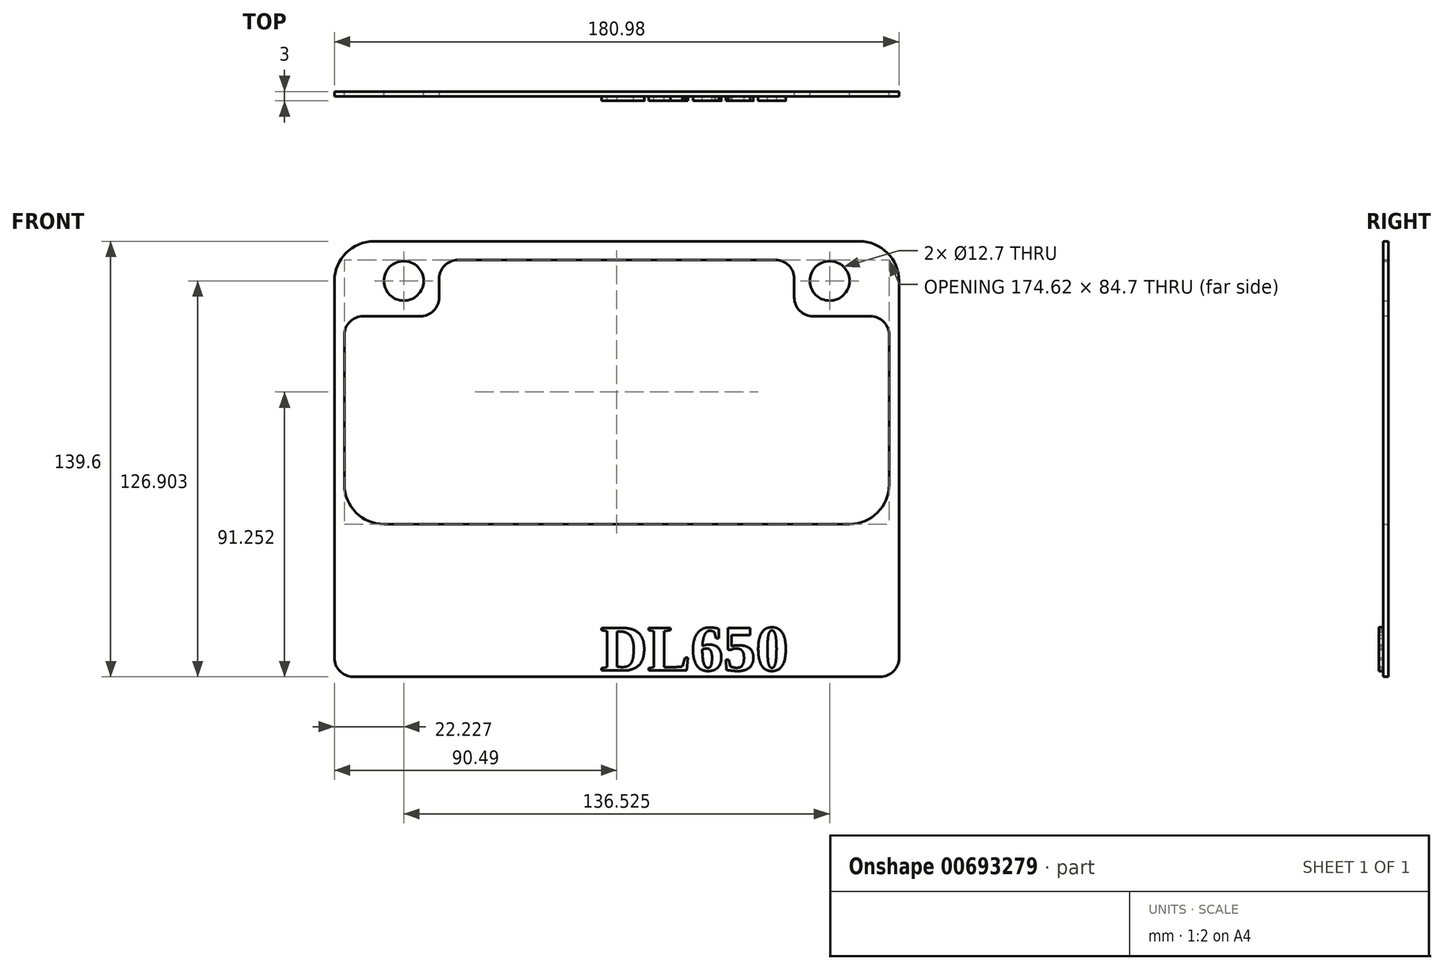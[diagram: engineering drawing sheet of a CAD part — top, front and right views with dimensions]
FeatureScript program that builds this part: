
annotation { "Feature Type Name" : "Feature", "Feature Type Description" : "" }
export const myFeature = defineFeature(function(context is Context, id is Id, definition is map)
    precondition{}
    {
        {
            var Q0;
            Q0=qCreatedBy(makeId("Front.planeOp"),FACE);
            var sketch = newSketch(context, id + "F0", { "sketchPlane" : qUnion([Q0])});
            skLineSegment(sketch, "E0", {"start": v(-77.79, 78) * mm, "end": v(77.79, 78) * mm});
            skLineSegment(sketch, "E1", {"start": v(-74.61, 44) * mm, "end": v(74.61, 44) * mm});
            skLineSegment(sketch, "E2", {"start": v(-90.49, -68.18) * mm, "end": v(-90.49, 65.3) * mm});
            skLineSegment(sketch, "E3", {"start": v(90.49, 65.3) * mm, "end": v(90.49, -55.07) * mm});
            skLineSegment(sketch, "E4", {"start": v(87.31, 31.3) * mm, "end": v(87.31, 0) * mm});
            skLineSegment(sketch, "E5", {"start": v(-87.31, -61.26) * mm, "end": v(-87.31, -36.3) * mm});
            skLineSegment(sketch, "E6", {"start": v(-29.21, -51.66) * mm, "end": v(-23.1, -50.51) * mm});
            skLineSegment(sketch, "E7", {"start": v(-23.1, -50.51) * mm, "end": v(-20.29, -50.51) * mm});
            skLineSegment(sketch, "E8", {"start": v(-20.29, -50.51) * mm, "end": v(-18.64, -50.51) * mm});
            skLineSegment(sketch, "E9", {"start": v(-18.64, -50.51) * mm, "end": v(-22.38, -52.6) * mm});
            skLineSegment(sketch, "E10", {"start": v(-22.38, -52.6) * mm, "end": v(-28.52, -54.74) * mm});
            skLineSegment(sketch, "E11", {"start": v(-28.52, -54.74) * mm, "end": v(-35.07, -55.94) * mm});
            skLineSegment(sketch, "E12", {"start": v(-35.07, -55.94) * mm, "end": v(-35.07, -58.79) * mm});
            skLineSegment(sketch, "E13", {"start": v(-35.07, -58.79) * mm, "end": v(-27.72, -61.77) * mm});
            skLineSegment(sketch, "E14", {"start": v(-27.72, -61.77) * mm, "end": v(-24.39, -63.12) * mm});
            skLineSegment(sketch, "E15", {"start": v(-24.39, -63.12) * mm, "end": v(-22.78, -62.57) * mm});
            skLineSegment(sketch, "E16", {"start": v(-22.78, -62.57) * mm, "end": v(-14.86, -59.1) * mm});
            skLineSegment(sketch, "E17", {"start": v(-14.86, -59.1) * mm, "end": v(-13.34, -57.8) * mm});
            skLineSegment(sketch, "E18", {"start": v(-13.34, -57.8) * mm, "end": v(-20.87, -57.8) * mm});
            skLineSegment(sketch, "E19", {"start": v(-20.87, -57.8) * mm, "end": v(-20.87, -55.05) * mm});
            skLineSegment(sketch, "E20", {"start": v(-20.87, -55.05) * mm, "end": v(-9.3, -55.27) * mm});
            skLineSegment(sketch, "E21", {"start": v(-9.3, -55.27) * mm, "end": v(-5.99, -52.6) * mm});
            skLineSegment(sketch, "E22", {"start": v(-5.99, -52.6) * mm, "end": v(-2.52, -52.6) * mm});
            skLineSegment(sketch, "E23", {"start": v(-2.52, -52.6) * mm, "end": v(-2.32, -55) * mm});
            skLineSegment(sketch, "E24", {"start": v(-2.32, -55) * mm, "end": v(2.72, -55) * mm});
            skLineSegment(sketch, "E25", {"start": v(2.72, -55) * mm, "end": v(1.05, -57.08) * mm});
            skLineSegment(sketch, "E26", {"start": v(1.05, -57.08) * mm, "end": v(-3.5, -57.08) * mm});
            skLineSegment(sketch, "E27", {"start": v(-3.5, -57.08) * mm, "end": v(-8.64, -62.21) * mm});
            skLineSegment(sketch, "E28", {"start": v(-8.64, -62.21) * mm, "end": v(-8.64, -63.64) * mm});
            skLineSegment(sketch, "E29", {"start": v(-8.64, -63.64) * mm, "end": v(-6.69, -63.64) * mm});
            skLineSegment(sketch, "E30", {"start": v(-6.69, -63.64) * mm, "end": v(2.22, -59.94) * mm});
            skLineSegment(sketch, "E31", {"start": v(2.22, -59.94) * mm, "end": v(5.6, -59.25) * mm});
            skLineSegment(sketch, "E32", {"start": v(5.6, -59.25) * mm, "end": v(12.9, -59.62) * mm});
            skLineSegment(sketch, "E33", {"start": v(12.9, -59.62) * mm, "end": v(13.98, -60.58) * mm});
            skLineSegment(sketch, "E34", {"start": v(13.98, -60.58) * mm, "end": v(13, -62.78) * mm});
            skLineSegment(sketch, "E35", {"start": v(13, -62.78) * mm, "end": v(12.55, -63.82) * mm});
            skLineSegment(sketch, "E36", {"start": v(12.55, -63.82) * mm, "end": v(13.6, -63.82) * mm});
            skLineSegment(sketch, "E37", {"start": v(13.6, -63.82) * mm, "end": v(15.7, -63.82) * mm});
            skLineSegment(sketch, "E38", {"start": v(15.7, -63.82) * mm, "end": v(22.1, -60.67) * mm});
            skLineSegment(sketch, "E39", {"start": v(22.1, -60.67) * mm, "end": v(24.65, -59.78) * mm});
            skLineSegment(sketch, "E40", {"start": v(24.65, -59.78) * mm, "end": v(27.62, -59.78) * mm});
            skLineSegment(sketch, "E41", {"start": v(27.62, -59.78) * mm, "end": v(30.1, -59.78) * mm});
            skLineSegment(sketch, "E42", {"start": v(30.1, -59.78) * mm, "end": v(31.7, -60) * mm});
            skLineSegment(sketch, "E43", {"start": v(29.74, -61.98) * mm, "end": v(27.27, -61.82) * mm});
            skLineSegment(sketch, "E44", {"start": v(27.27, -61.82) * mm, "end": v(25.05, -62.7) * mm});
            skLineSegment(sketch, "E45", {"start": v(25.05, -62.7) * mm, "end": v(23.07, -63.82) * mm});
            skLineSegment(sketch, "E46", {"start": v(23.07, -63.82) * mm, "end": v(23.07, -64.66) * mm});
            skLineSegment(sketch, "E47", {"start": v(23.07, -64.66) * mm, "end": v(23.64, -65.45) * mm});
            skLineSegment(sketch, "E48", {"start": v(23.64, -65.45) * mm, "end": v(24.65, -65.45) * mm});
            skLineSegment(sketch, "E49", {"start": v(24.65, -65.45) * mm, "end": v(27.23, -65.45) * mm});
            skLineSegment(sketch, "E50", {"start": v(27.23, -65.45) * mm, "end": v(28.75, -65.45) * mm});
            skLineSegment(sketch, "E51", {"start": v(28.75, -65.45) * mm, "end": v(28.75, -65.45) * mm});
            skLineSegment(sketch, "E52", {"start": v(28.75, -65.45) * mm, "end": v(30.56, -64.83) * mm});
            skLineSegment(sketch, "E53", {"start": v(30.56, -64.83) * mm, "end": v(31.39, -63.37) * mm});
            skLineSegment(sketch, "E54", {"start": v(31.39, -63.37) * mm, "end": v(30.32, -62.47) * mm});
            skLineSegment(sketch, "E55", {"start": v(30.32, -62.47) * mm, "end": v(29.74, -61.98) * mm});
            skLineSegment(sketch, "E56", {"start": v(31.7, -60) * mm, "end": v(37.4, -60) * mm});
            skLineSegment(sketch, "E57", {"start": v(37.4, -60) * mm, "end": v(38.4, -61.18) * mm});
            skLineSegment(sketch, "E58", {"start": v(38.4, -61.18) * mm, "end": v(39.02, -62.98) * mm});
            skLineSegment(sketch, "E59", {"start": v(39.02, -62.98) * mm, "end": v(39.02, -63.65) * mm});
            skLineSegment(sketch, "E60", {"start": v(39.02, -63.65) * mm, "end": v(41.33, -62.76) * mm});
            skLineSegment(sketch, "E61", {"start": v(41.33, -62.76) * mm, "end": v(44.09, -61.68) * mm});
            skLineSegment(sketch, "E62", {"start": v(44.09, -61.68) * mm, "end": v(47.27, -60.44) * mm});
            skLineSegment(sketch, "E63", {"start": v(47.27, -60.44) * mm, "end": v(50.76, -59.08) * mm});
            skLineSegment(sketch, "E64", {"start": v(50.76, -59.08) * mm, "end": v(54.5, -59.08) * mm});
            skLineSegment(sketch, "E65", {"start": v(54.5, -59.08) * mm, "end": v(54.6, -61.64) * mm});
            skLineSegment(sketch, "E66", {"start": v(54.6, -61.64) * mm, "end": v(54.63, -62.25) * mm});
            skLineSegment(sketch, "E67", {"start": v(54.63, -62.25) * mm, "end": v(61.4, -59.33) * mm});
            skLineSegment(sketch, "E68", {"start": v(61.4, -59.33) * mm, "end": v(63.14, -58.58) * mm});
            skLineSegment(sketch, "E69", {"start": v(63.14, -58.58) * mm, "end": v(66.16, -58.58) * mm});
            skLineSegment(sketch, "E70", {"start": v(66.16, -58.58) * mm, "end": v(67, -58.91) * mm});
            skLineSegment(sketch, "E71", {"start": v(67, -58.91) * mm, "end": v(67, -60.93) * mm});
            skLineSegment(sketch, "E72", {"start": v(67, -60.93) * mm, "end": v(67, -61.6) * mm});
            skLineSegment(sketch, "E73", {"start": v(67, -61.6) * mm, "end": v(67, -62.28) * mm});
            skLineSegment(sketch, "E74", {"start": v(67, -62.28) * mm, "end": v(75.87, -58.62) * mm});
            skLineSegment(sketch, "E75", {"start": v(75.87, -58.62) * mm, "end": v(78.57, -58.62) * mm});
            skLineSegment(sketch, "E76", {"start": v(78.57, -58.62) * mm, "end": v(78.57, -61.4) * mm});
            skLineSegment(sketch, "E77", {"start": v(78.57, -61.4) * mm, "end": v(77.64, -63.25) * mm});
            skLineSegment(sketch, "E78", {"start": v(77.64, -63.25) * mm, "end": v(80.4, -62.97) * mm});
            skLineSegment(sketch, "E79", {"start": v(80.4, -62.97) * mm, "end": v(80.4, -62.97) * mm});
            skLineSegment(sketch, "E80", {"start": v(-82, -51.28) * mm, "end": v(-82, -52.51) * mm});
            skLineSegment(sketch, "E81", {"start": v(-82, -52.51) * mm, "end": v(-85.85, -58.12) * mm});
            skLineSegment(sketch, "E82", {"start": v(-85.85, -58.12) * mm, "end": v(-87.31, -61.26) * mm});
            skLineSegment(sketch, "E83", {"start": v(-80.53, -66.46) * mm, "end": v(-80.53, -67.97) * mm});
            skArc(sketch, "E84", {"start": v(-80.53, -67.6) * mm, "mid": v(-80.07, -68.53) * mm, "end": v(-79.07, -68.25) * mm});
            skLineSegment(sketch, "E85", {"start": v(-79.07, -68.25) * mm, "end": v(-73.01, -63.37) * mm});
            skLineSegment(sketch, "E86", {"start": v(-73.01, -63.37) * mm, "end": v(-64.95, -57.96) * mm});
            skLineSegment(sketch, "E87", {"start": v(-64.95, -57.96) * mm, "end": v(-56.54, -52.32) * mm});
            skLineSegment(sketch, "E88", {"start": v(-56.54, -52.32) * mm, "end": v(-43.18, -46.47) * mm});
            skLineSegment(sketch, "E89", {"start": v(-43.18, -46.47) * mm, "end": v(-41.77, -46.08) * mm});
            skLineSegment(sketch, "E90", {"start": v(-41.77, -46.08) * mm, "end": v(-38.67, -45.2) * mm});
            skLineSegment(sketch, "E91", {"start": v(-38.67, -45.2) * mm, "end": v(-31.98, -45.2) * mm});
            skLineSegment(sketch, "E92", {"start": v(-31.98, -45.2) * mm, "end": v(-31.98, -46.08) * mm});
            skLineSegment(sketch, "E93", {"start": v(-31.98, -46.08) * mm, "end": v(-37.08, -47.84) * mm});
            skLineSegment(sketch, "E94", {"start": v(-37.08, -47.84) * mm, "end": v(-42.97, -49.87) * mm});
            skLineSegment(sketch, "E95", {"start": v(-42.97, -49.87) * mm, "end": v(-54.97, -57.27) * mm});
            skLineSegment(sketch, "E96", {"start": v(-54.97, -57.27) * mm, "end": v(-58.2, -60.02) * mm});
            skLineSegment(sketch, "E97", {"start": v(-58.2, -60.02) * mm, "end": v(-58.2, -61.31) * mm});
            skLineSegment(sketch, "E98", {"start": v(-58.2, -61.31) * mm, "end": v(-49.34, -61.31) * mm});
            skLineSegment(sketch, "E99", {"start": v(-56.96, -68.6) * mm, "end": v(-54.55, -68.27) * mm});
            skLineSegment(sketch, "E100", {"start": v(-85.54, -78) * mm, "end": v(-81.5, -78) * mm});
            skLineSegment(sketch, "E101", {"start": v(-90.39, -73.88) * mm, "end": v(-85.54, -77.1) * mm});
            skLineSegment(sketch, "E102", {"start": v(-85.54, -77.1) * mm, "end": v(-85.54, -78) * mm});
            skLineSegment(sketch, "E103", {"start": v(-84.43, -51.28) * mm, "end": v(-84.43, -49.97) * mm});
            skLineSegment(sketch, "E104", {"start": v(-84.43, -49.97) * mm, "end": v(-76.06, -46.38) * mm});
            skLineSegment(sketch, "E105", {"start": v(-76.06, -46.38) * mm, "end": v(-70.01, -46.38) * mm});
            skLineSegment(sketch, "E106", {"start": v(-70, -48.96) * mm, "end": v(-80.53, -66.46) * mm});
            skLineSegment(sketch, "E107", {"start": v(-84.43, -51.28) * mm, "end": v(-82, -51.28) * mm});
            skArc(sketch, "E108", {"start": v(-70, -48.96) * mm, "mid": v(-69.56, -47.67) * mm, "end": v(-70.01, -46.38) * mm});
            skLineSegment(sketch, "E109", {"start": v(-33.04, -63.57) * mm, "end": v(-42.47, -59.8) * mm});
            skLineSegment(sketch, "E110", {"start": v(-45.02, -57.68) * mm, "end": v(-43.38, -56.24) * mm});
            skLineSegment(sketch, "E111", {"start": v(-43.38, -56.24) * mm, "end": v(-38.17, -53.84) * mm});
            skLineSegment(sketch, "E112", {"start": v(-38.17, -53.84) * mm, "end": v(-32.55, -52.47) * mm});
            skLineSegment(sketch, "E113", {"start": v(-32.55, -52.47) * mm, "end": v(-29.21, -51.66) * mm});
            skArc(sketch, "E114", {"start": v(-45.02, -57.68) * mm, "mid": v(-43.94, -58.96) * mm, "end": v(-42.47, -59.8) * mm});
            skArc(sketch, "E115", {"start": v(-32.75, -65.3) * mm, "mid": v(-32.5, -64.25) * mm, "end": v(-33.27, -63.48) * mm});
            skLineSegment(sketch, "E116", {"start": v(82.78, -65.37) * mm, "end": v(76.07, -67.34) * mm});
            skLineSegment(sketch, "E117", {"start": v(76.07, -67.34) * mm, "end": v(71.6, -67.34) * mm});
            skLineSegment(sketch, "E118", {"start": v(71.6, -67.34) * mm, "end": v(72.25, -63.16) * mm});
            skLineSegment(sketch, "E119", {"start": v(72.25, -63.16) * mm, "end": v(62.42, -66.98) * mm});
            skLineSegment(sketch, "E120", {"start": v(62.42, -66.98) * mm, "end": v(57.9, -66.98) * mm});
            skLineSegment(sketch, "E121", {"start": v(57.9, -66.98) * mm, "end": v(59.54, -64.28) * mm});
            skLineSegment(sketch, "E122", {"start": v(59.54, -64.28) * mm, "end": v(58.84, -63.4) * mm});
            skLineSegment(sketch, "E123", {"start": v(58.84, -63.4) * mm, "end": v(57.37, -63.4) * mm});
            skLineSegment(sketch, "E124", {"start": v(57.37, -63.4) * mm, "end": v(49.3, -67.45) * mm});
            skLineSegment(sketch, "E125", {"start": v(49.3, -67.45) * mm, "end": v(45.66, -67.45) * mm});
            skLineSegment(sketch, "E126", {"start": v(45.66, -67.45) * mm, "end": v(44.96, -65.99) * mm});
            skLineSegment(sketch, "E127", {"start": v(44.96, -65.99) * mm, "end": v(46.72, -64.4) * mm});
            skLineSegment(sketch, "E128", {"start": v(46.72, -64.4) * mm, "end": v(46.43, -63.45) * mm});
            skLineSegment(sketch, "E129", {"start": v(46.43, -63.45) * mm, "end": v(45.22, -63.45) * mm});
            skLineSegment(sketch, "E130", {"start": v(45.22, -63.45) * mm, "end": v(41.02, -65.5) * mm});
            skLineSegment(sketch, "E131", {"start": v(41.02, -65.5) * mm, "end": v(39.57, -66.2) * mm});
            skLineSegment(sketch, "E132", {"start": v(39.57, -66.2) * mm, "end": v(37.64, -67.14) * mm});
            skLineSegment(sketch, "E133", {"start": v(37.64, -67.14) * mm, "end": v(31, -67.9) * mm});
            skLineSegment(sketch, "E134", {"start": v(31, -67.9) * mm, "end": v(27.87, -68.25) * mm});
            skLineSegment(sketch, "E135", {"start": v(27.87, -68.25) * mm, "end": v(22.36, -68.25) * mm});
            skLineSegment(sketch, "E136", {"start": v(22.36, -68.25) * mm, "end": v(20.07, -68.25) * mm});
            skLineSegment(sketch, "E137", {"start": v(20.07, -68.25) * mm, "end": v(18.41, -66.61) * mm});
            skLineSegment(sketch, "E138", {"start": v(18.41, -66.61) * mm, "end": v(17.72, -65.92) * mm});
            skLineSegment(sketch, "E139", {"start": v(17.72, -65.92) * mm, "end": v(16.92, -65.92) * mm});
            skLineSegment(sketch, "E140", {"start": v(16.92, -65.92) * mm, "end": v(14.63, -65.92) * mm});
            skLineSegment(sketch, "E141", {"start": v(14.63, -65.92) * mm, "end": v(7.74, -67.52) * mm});
            skLineSegment(sketch, "E142", {"start": v(7.74, -67.52) * mm, "end": v(6.36, -67.52) * mm});
            skLineSegment(sketch, "E143", {"start": v(6.36, -67.52) * mm, "end": v(6.36, -65.44) * mm});
            skLineSegment(sketch, "E144", {"start": v(6.36, -65.44) * mm, "end": v(7.32, -64.7) * mm});
            skLineSegment(sketch, "E145", {"start": v(7.32, -64.7) * mm, "end": v(8.44, -63.84) * mm});
            skLineSegment(sketch, "E146", {"start": v(8.44, -63.84) * mm, "end": v(8.38, -62.61) * mm});
            skLineSegment(sketch, "E147", {"start": v(8.38, -62.61) * mm, "end": v(6.68, -62.03) * mm});
            skLineSegment(sketch, "E148", {"start": v(6.68, -62.03) * mm, "end": v(4.17, -62.03) * mm});
            skLineSegment(sketch, "E149", {"start": v(4.17, -62.03) * mm, "end": v(0.97, -63.79) * mm});
            skLineSegment(sketch, "E150", {"start": v(0.97, -63.79) * mm, "end": v(-9.74, -67.36) * mm});
            skLineSegment(sketch, "E151", {"start": v(-9.74, -67.36) * mm, "end": v(-12.94, -67.36) * mm});
            skLineSegment(sketch, "E152", {"start": v(-12.94, -67.36) * mm, "end": v(-15.34, -67.36) * mm});
            skLineSegment(sketch, "E153", {"start": v(-15.34, -67.36) * mm, "end": v(-15.34, -62.83) * mm});
            skLineSegment(sketch, "E154", {"start": v(-15.34, -62.83) * mm, "end": v(-15.98, -62.83) * mm});
            skLineSegment(sketch, "E155", {"start": v(-15.98, -62.83) * mm, "end": v(-20.25, -64.96) * mm});
            skLineSegment(sketch, "E156", {"start": v(-20.25, -64.96) * mm, "end": v(-34.94, -68.98) * mm});
            skLineSegment(sketch, "E157", {"start": v(-34.94, -68.98) * mm, "end": v(-42.63, -70.75) * mm});
            skLineSegment(sketch, "E158", {"start": v(-42.63, -70.75) * mm, "end": v(-45.78, -71.48) * mm});
            skLineSegment(sketch, "E159", {"start": v(-45.78, -71.48) * mm, "end": v(-48.87, -72.2) * mm});
            skLineSegment(sketch, "E160", {"start": v(-48.87, -72.2) * mm, "end": v(-53.53, -71.11) * mm});
            skLineSegment(sketch, "E161", {"start": v(-53.53, -71.11) * mm, "end": v(-56.96, -68.6) * mm});
            skLineSegment(sketch, "E162", {"start": v(-90.49, -68.18) * mm, "end": v(-90.39, -73.88) * mm});
            skCircle(sketch, "E163", {"center": v(-68.26, 65.3) * mm, "radius": 6.35 * mm});
            skCircle(sketch, "E164", {"center": v(68.26, 65.3) * mm, "radius": 6.35 * mm});
            skLineSegment(sketch, "E165", {"start": v(-54.55, -64.45) * mm, "end": v(-54.55, -68.27) * mm});
            skLineSegment(sketch, "E166", {"start": v(-49.34, -61.31) * mm, "end": v(-49.34, -67.56) * mm});
            skLineSegment(sketch, "E167", {"start": v(-54.55, -64.45) * mm, "end": v(-59.25, -64.45) * mm});
            skLineSegment(sketch, "E168", {"start": v(-59.25, -64.45) * mm, "end": v(-62.72, -64.2) * mm});
            skLineSegment(sketch, "E169", {"start": v(-62.72, -64.2) * mm, "end": v(-63.8, -64.11) * mm});
            skLineSegment(sketch, "E170", {"start": v(-63.8, -64.11) * mm, "end": v(-79.82, -76.84) * mm});
            skLineSegment(sketch, "E171", {"start": v(-79.82, -76.84) * mm, "end": v(-81.5, -78) * mm});
            skLineSegment(sketch, "E172", {"start": v(-49.34, -67.56) * mm, "end": v(-32.75, -65.3) * mm});
            skArc(sketch, "E173", {"start": v(-74.61, 44) * mm, "mid": v(-83.6, 40.29) * mm, "end": v(-87.31, 31.3) * mm});
            skArc(sketch, "E174", {"start": v(87.31, 31.3) * mm, "mid": v(83.6, 40.29) * mm, "end": v(74.61, 44) * mm});
            skArc(sketch, "E175", {"start": v(-77.79, 78) * mm, "mid": v(-86.77, 74.28) * mm, "end": v(-90.49, 65.3) * mm});
            skArc(sketch, "E176", {"start": v(90.49, 65.3) * mm, "mid": v(86.77, 74.28) * mm, "end": v(77.79, 78) * mm});
            skLineSegment(sketch, "E177", {"start": v(-74.61, -23.6) * mm, "end": v(74.61, -23.6) * mm});
            skLineSegment(sketch, "E178", {"start": v(-74.61, -12.7) * mm, "end": v(74.61, -12.7) * mm});
            skLineSegment(sketch, "E179", {"start": v(-87.31, 0) * mm, "end": v(-87.31, 31.3) * mm});
            skLineSegment(sketch, "E180", {"start": v(87.31, -36.3) * mm, "end": v(87.31, -53.65) * mm});
            skArc(sketch, "E181", {"start": v(-87.31, 0) * mm, "mid": v(-83.6, -8.98) * mm, "end": v(-74.61, -12.7) * mm});
            skArc(sketch, "E182", {"start": v(-74.61, -23.6) * mm, "mid": v(-83.6, -27.32) * mm, "end": v(-87.31, -36.3) * mm});
            skArc(sketch, "E183", {"start": v(87.31, -36.3) * mm, "mid": v(83.6, -27.32) * mm, "end": v(74.61, -23.6) * mm});
            skArc(sketch, "E184", {"start": v(74.61, -12.7) * mm, "mid": v(83.6, -8.98) * mm, "end": v(87.31, 0) * mm});
            skLineSegment(sketch, "E185", {"start": v(0, 78) * mm, "end": v(0, 44) * mm, "construction": true});
            skLineSegment(sketch, "E186", {"start": v(0, 0) * mm, "end": v(0, -23.6) * mm, "construction": true});
            skArc(sketch, "E187", {"start": v(80.4, -62.97) * mm, "mid": v(85.4, -59.45) * mm, "end": v(87.31, -53.65) * mm});
            skArc(sketch, "E188", {"start": v(82.78, -65.37) * mm, "mid": v(88.35, -61.5) * mm, "end": v(90.49, -55.07) * mm});
            skSolve(sketch);
        }
        {
            var Q0;
            Q0 = qSketchRegion(id + "F0", true);
            extrude(context, id + "F1", {"entities" : qUnion([Q0]), "depth" : 1.6 * mm, "offsetDistance" : 25 * mm});
        }
        {
            var Q0;
            Q0=makeQuery(id+"F1.opExtrude","CAP_FACE",FACE,{"disambiguationData":[OSD([sQuery(id+"F0.wireOp",EDGE,"E0"),sQuery(id+"F0.wireOp",EDGE,"E1"),sQuery(id+"F0.wireOp",EDGE,"E2"),sQuery(id+"F0.wireOp",EDGE,"E3"),sQuery(id+"F0.wireOp",EDGE,"E4"),sQuery(id+"F0.wireOp",EDGE,"E5"),sQuery(id+"F0.wireOp",EDGE,"E6"),sQuery(id+"F0.wireOp",EDGE,"E7"),sQuery(id+"F0.wireOp",EDGE,"E8"),sQuery(id+"F0.wireOp",EDGE,"E9"),sQuery(id+"F0.wireOp",EDGE,"E10"),sQuery(id+"F0.wireOp",EDGE,"E11"),sQuery(id+"F0.wireOp",EDGE,"E12"),sQuery(id+"F0.wireOp",EDGE,"E13"),sQuery(id+"F0.wireOp",EDGE,"E14"),sQuery(id+"F0.wireOp",EDGE,"E15"),sQuery(id+"F0.wireOp",EDGE,"E16"),sQuery(id+"F0.wireOp",EDGE,"E17"),sQuery(id+"F0.wireOp",EDGE,"E18"),sQuery(id+"F0.wireOp",EDGE,"E19"),sQuery(id+"F0.wireOp",EDGE,"E20"),sQuery(id+"F0.wireOp",EDGE,"E21"),sQuery(id+"F0.wireOp",EDGE,"E22"),sQuery(id+"F0.wireOp",EDGE,"E23"),sQuery(id+"F0.wireOp",EDGE,"E24"),sQuery(id+"F0.wireOp",EDGE,"E25"),sQuery(id+"F0.wireOp",EDGE,"E26"),sQuery(id+"F0.wireOp",EDGE,"E27"),sQuery(id+"F0.wireOp",EDGE,"E28"),sQuery(id+"F0.wireOp",EDGE,"E29"),sQuery(id+"F0.wireOp",EDGE,"E30"),sQuery(id+"F0.wireOp",EDGE,"E31"),sQuery(id+"F0.wireOp",EDGE,"E32"),sQuery(id+"F0.wireOp",EDGE,"E33"),sQuery(id+"F0.wireOp",EDGE,"E34"),sQuery(id+"F0.wireOp",EDGE,"E35"),sQuery(id+"F0.wireOp",EDGE,"E36"),sQuery(id+"F0.wireOp",EDGE,"E37"),sQuery(id+"F0.wireOp",EDGE,"E38"),sQuery(id+"F0.wireOp",EDGE,"E39"),sQuery(id+"F0.wireOp",EDGE,"E40"),sQuery(id+"F0.wireOp",EDGE,"E41"),sQuery(id+"F0.wireOp",EDGE,"E42"),sQuery(id+"F0.wireOp",EDGE,"E43"),sQuery(id+"F0.wireOp",EDGE,"E44"),sQuery(id+"F0.wireOp",EDGE,"E45"),sQuery(id+"F0.wireOp",EDGE,"E46"),sQuery(id+"F0.wireOp",EDGE,"E47"),sQuery(id+"F0.wireOp",EDGE,"E48"),sQuery(id+"F0.wireOp",EDGE,"E49"),sQuery(id+"F0.wireOp",EDGE,"E50"),sQuery(id+"F0.wireOp",EDGE,"E52"),sQuery(id+"F0.wireOp",EDGE,"E53"),sQuery(id+"F0.wireOp",EDGE,"E54"),sQuery(id+"F0.wireOp",EDGE,"E55"),sQuery(id+"F0.wireOp",EDGE,"E56"),sQuery(id+"F0.wireOp",EDGE,"E57"),sQuery(id+"F0.wireOp",EDGE,"E58"),sQuery(id+"F0.wireOp",EDGE,"E59"),sQuery(id+"F0.wireOp",EDGE,"E60"),sQuery(id+"F0.wireOp",EDGE,"E61"),sQuery(id+"F0.wireOp",EDGE,"E62"),sQuery(id+"F0.wireOp",EDGE,"E63"),sQuery(id+"F0.wireOp",EDGE,"E64"),sQuery(id+"F0.wireOp",EDGE,"E65"),sQuery(id+"F0.wireOp",EDGE,"E66"),sQuery(id+"F0.wireOp",EDGE,"E67"),sQuery(id+"F0.wireOp",EDGE,"E68"),sQuery(id+"F0.wireOp",EDGE,"E69"),sQuery(id+"F0.wireOp",EDGE,"E70"),sQuery(id+"F0.wireOp",EDGE,"E71"),sQuery(id+"F0.wireOp",EDGE,"E72"),sQuery(id+"F0.wireOp",EDGE,"E73"),sQuery(id+"F0.wireOp",EDGE,"E74"),sQuery(id+"F0.wireOp",EDGE,"E75"),sQuery(id+"F0.wireOp",EDGE,"E76"),sQuery(id+"F0.wireOp",EDGE,"E77"),sQuery(id+"F0.wireOp",EDGE,"E78"),sQuery(id+"F0.wireOp",EDGE,"E80"),sQuery(id+"F0.wireOp",EDGE,"E81"),sQuery(id+"F0.wireOp",EDGE,"E82"),sQuery(id+"F0.wireOp",EDGE,"E83"),sQuery(id+"F0.wireOp",EDGE,"E84"),sQuery(id+"F0.wireOp",EDGE,"E85"),sQuery(id+"F0.wireOp",EDGE,"E86"),sQuery(id+"F0.wireOp",EDGE,"E87"),sQuery(id+"F0.wireOp",EDGE,"E88"),sQuery(id+"F0.wireOp",EDGE,"E89"),sQuery(id+"F0.wireOp",EDGE,"E90"),sQuery(id+"F0.wireOp",EDGE,"E91"),sQuery(id+"F0.wireOp",EDGE,"E92"),sQuery(id+"F0.wireOp",EDGE,"E93"),sQuery(id+"F0.wireOp",EDGE,"E94"),sQuery(id+"F0.wireOp",EDGE,"E95"),sQuery(id+"F0.wireOp",EDGE,"E96"),sQuery(id+"F0.wireOp",EDGE,"E97"),sQuery(id+"F0.wireOp",EDGE,"E98"),sQuery(id+"F0.wireOp",EDGE,"E99"),sQuery(id+"F0.wireOp",EDGE,"E100"),sQuery(id+"F0.wireOp",EDGE,"E101"),sQuery(id+"F0.wireOp",EDGE,"E102"),sQuery(id+"F0.wireOp",EDGE,"E103"),sQuery(id+"F0.wireOp",EDGE,"E104"),sQuery(id+"F0.wireOp",EDGE,"E105"),sQuery(id+"F0.wireOp",EDGE,"E106"),sQuery(id+"F0.wireOp",EDGE,"E107"),sQuery(id+"F0.wireOp",EDGE,"E108"),sQuery(id+"F0.wireOp",EDGE,"E109"),sQuery(id+"F0.wireOp",EDGE,"E110"),sQuery(id+"F0.wireOp",EDGE,"E111"),sQuery(id+"F0.wireOp",EDGE,"E112"),sQuery(id+"F0.wireOp",EDGE,"E113"),sQuery(id+"F0.wireOp",EDGE,"E114"),sQuery(id+"F0.wireOp",EDGE,"E115"),sQuery(id+"F0.wireOp",EDGE,"E116"),sQuery(id+"F0.wireOp",EDGE,"E117"),sQuery(id+"F0.wireOp",EDGE,"E118"),sQuery(id+"F0.wireOp",EDGE,"E119"),sQuery(id+"F0.wireOp",EDGE,"E120"),sQuery(id+"F0.wireOp",EDGE,"E121"),sQuery(id+"F0.wireOp",EDGE,"E122"),sQuery(id+"F0.wireOp",EDGE,"E123"),sQuery(id+"F0.wireOp",EDGE,"E124"),sQuery(id+"F0.wireOp",EDGE,"E125"),sQuery(id+"F0.wireOp",EDGE,"E126"),sQuery(id+"F0.wireOp",EDGE,"E127"),sQuery(id+"F0.wireOp",EDGE,"E128"),sQuery(id+"F0.wireOp",EDGE,"E129"),sQuery(id+"F0.wireOp",EDGE,"E130"),sQuery(id+"F0.wireOp",EDGE,"E131"),sQuery(id+"F0.wireOp",EDGE,"E132"),sQuery(id+"F0.wireOp",EDGE,"E133"),sQuery(id+"F0.wireOp",EDGE,"E134"),sQuery(id+"F0.wireOp",EDGE,"E135"),sQuery(id+"F0.wireOp",EDGE,"E136"),sQuery(id+"F0.wireOp",EDGE,"E137"),sQuery(id+"F0.wireOp",EDGE,"E138"),sQuery(id+"F0.wireOp",EDGE,"E139"),sQuery(id+"F0.wireOp",EDGE,"E140"),sQuery(id+"F0.wireOp",EDGE,"E141"),sQuery(id+"F0.wireOp",EDGE,"E142"),sQuery(id+"F0.wireOp",EDGE,"E143"),sQuery(id+"F0.wireOp",EDGE,"E144"),sQuery(id+"F0.wireOp",EDGE,"E145"),sQuery(id+"F0.wireOp",EDGE,"E146"),sQuery(id+"F0.wireOp",EDGE,"E147"),sQuery(id+"F0.wireOp",EDGE,"E148"),sQuery(id+"F0.wireOp",EDGE,"E149"),sQuery(id+"F0.wireOp",EDGE,"E150"),sQuery(id+"F0.wireOp",EDGE,"E151"),sQuery(id+"F0.wireOp",EDGE,"E152"),sQuery(id+"F0.wireOp",EDGE,"E153"),sQuery(id+"F0.wireOp",EDGE,"E154"),sQuery(id+"F0.wireOp",EDGE,"E155"),sQuery(id+"F0.wireOp",EDGE,"E156"),sQuery(id+"F0.wireOp",EDGE,"E157"),sQuery(id+"F0.wireOp",EDGE,"E158"),sQuery(id+"F0.wireOp",EDGE,"E159"),sQuery(id+"F0.wireOp",EDGE,"E160"),sQuery(id+"F0.wireOp",EDGE,"E161"),sQuery(id+"F0.wireOp",EDGE,"E162"),sQuery(id+"F0.wireOp",EDGE,"E163"),sQuery(id+"F0.wireOp",EDGE,"E164"),sQuery(id+"F0.wireOp",EDGE,"E165"),sQuery(id+"F0.wireOp",EDGE,"E166"),sQuery(id+"F0.wireOp",EDGE,"E167"),sQuery(id+"F0.wireOp",EDGE,"E168"),sQuery(id+"F0.wireOp",EDGE,"E169"),sQuery(id+"F0.wireOp",EDGE,"E170"),sQuery(id+"F0.wireOp",EDGE,"E171"),sQuery(id+"F0.wireOp",EDGE,"E172"),sQuery(id+"F0.wireOp",EDGE,"E173"),sQuery(id+"F0.wireOp",EDGE,"E174"),sQuery(id+"F0.wireOp",EDGE,"E175"),sQuery(id+"F0.wireOp",EDGE,"E176"),sQuery(id+"F0.wireOp",EDGE,"E177"),sQuery(id+"F0.wireOp",EDGE,"E178"),sQuery(id+"F0.wireOp",EDGE,"E179"),sQuery(id+"F0.wireOp",EDGE,"E180"),sQuery(id+"F0.wireOp",EDGE,"E181"),sQuery(id+"F0.wireOp",EDGE,"E182"),sQuery(id+"F0.wireOp",EDGE,"E183"),sQuery(id+"F0.wireOp",EDGE,"E184"),sQuery(id+"F0.wireOp",EDGE,"E187"),sQuery(id+"F0.wireOp",EDGE,"E188")])],"isStart":false});
            var sketch = newSketch(context, id + "F2", { "sketchPlane" : qUnion([Q0])});
            skLineSegment(sketch, "E189.bottom", {"start": v(-95.82, -23.6) * mm, "end": v(99.75, -23.6) * mm});
            skLineSegment(sketch, "E189.top", {"start": v(-95.82, -81.55) * mm, "end": v(99.75, -81.55) * mm});
            skLineSegment(sketch, "E189.left", {"start": v(-95.82, -23.6) * mm, "end": v(-95.82, -81.55) * mm});
            skLineSegment(sketch, "E189.right", {"start": v(99.75, -23.6) * mm, "end": v(99.75, -81.55) * mm});
            skSolve(sketch);
        }
        {
            var Q0;
            Q0 = qSketchRegion(id + "F2", true);
            extrude(context, id + "F3", {"entities" : qUnion([Q0]), "operationType" : NewBodyOperationType.REMOVE, "oppositeDirection" : true, "depth" : 25 * mm, "offsetDistance" : 25 * mm});
        }
        {
            var Q0;
            Q0=makeQuery(id+"F1.opExtrude","CAP_FACE",FACE,{"disambiguationData":[OSD([sQuery(id+"F0.wireOp",EDGE,"E0"),sQuery(id+"F0.wireOp",EDGE,"E1"),sQuery(id+"F0.wireOp",EDGE,"E2"),sQuery(id+"F0.wireOp",EDGE,"E3"),sQuery(id+"F0.wireOp",EDGE,"E4"),sQuery(id+"F0.wireOp",EDGE,"E5"),sQuery(id+"F0.wireOp",EDGE,"E6"),sQuery(id+"F0.wireOp",EDGE,"E7"),sQuery(id+"F0.wireOp",EDGE,"E8"),sQuery(id+"F0.wireOp",EDGE,"E9"),sQuery(id+"F0.wireOp",EDGE,"E10"),sQuery(id+"F0.wireOp",EDGE,"E11"),sQuery(id+"F0.wireOp",EDGE,"E12"),sQuery(id+"F0.wireOp",EDGE,"E13"),sQuery(id+"F0.wireOp",EDGE,"E14"),sQuery(id+"F0.wireOp",EDGE,"E15"),sQuery(id+"F0.wireOp",EDGE,"E16"),sQuery(id+"F0.wireOp",EDGE,"E17"),sQuery(id+"F0.wireOp",EDGE,"E18"),sQuery(id+"F0.wireOp",EDGE,"E19"),sQuery(id+"F0.wireOp",EDGE,"E20"),sQuery(id+"F0.wireOp",EDGE,"E21"),sQuery(id+"F0.wireOp",EDGE,"E22"),sQuery(id+"F0.wireOp",EDGE,"E23"),sQuery(id+"F0.wireOp",EDGE,"E24"),sQuery(id+"F0.wireOp",EDGE,"E25"),sQuery(id+"F0.wireOp",EDGE,"E26"),sQuery(id+"F0.wireOp",EDGE,"E27"),sQuery(id+"F0.wireOp",EDGE,"E28"),sQuery(id+"F0.wireOp",EDGE,"E29"),sQuery(id+"F0.wireOp",EDGE,"E30"),sQuery(id+"F0.wireOp",EDGE,"E31"),sQuery(id+"F0.wireOp",EDGE,"E32"),sQuery(id+"F0.wireOp",EDGE,"E33"),sQuery(id+"F0.wireOp",EDGE,"E34"),sQuery(id+"F0.wireOp",EDGE,"E35"),sQuery(id+"F0.wireOp",EDGE,"E36"),sQuery(id+"F0.wireOp",EDGE,"E37"),sQuery(id+"F0.wireOp",EDGE,"E38"),sQuery(id+"F0.wireOp",EDGE,"E39"),sQuery(id+"F0.wireOp",EDGE,"E40"),sQuery(id+"F0.wireOp",EDGE,"E41"),sQuery(id+"F0.wireOp",EDGE,"E42"),sQuery(id+"F0.wireOp",EDGE,"E43"),sQuery(id+"F0.wireOp",EDGE,"E44"),sQuery(id+"F0.wireOp",EDGE,"E45"),sQuery(id+"F0.wireOp",EDGE,"E46"),sQuery(id+"F0.wireOp",EDGE,"E47"),sQuery(id+"F0.wireOp",EDGE,"E48"),sQuery(id+"F0.wireOp",EDGE,"E49"),sQuery(id+"F0.wireOp",EDGE,"E50"),sQuery(id+"F0.wireOp",EDGE,"E52"),sQuery(id+"F0.wireOp",EDGE,"E53"),sQuery(id+"F0.wireOp",EDGE,"E54"),sQuery(id+"F0.wireOp",EDGE,"E55"),sQuery(id+"F0.wireOp",EDGE,"E56"),sQuery(id+"F0.wireOp",EDGE,"E57"),sQuery(id+"F0.wireOp",EDGE,"E58"),sQuery(id+"F0.wireOp",EDGE,"E59"),sQuery(id+"F0.wireOp",EDGE,"E60"),sQuery(id+"F0.wireOp",EDGE,"E61"),sQuery(id+"F0.wireOp",EDGE,"E62"),sQuery(id+"F0.wireOp",EDGE,"E63"),sQuery(id+"F0.wireOp",EDGE,"E64"),sQuery(id+"F0.wireOp",EDGE,"E65"),sQuery(id+"F0.wireOp",EDGE,"E66"),sQuery(id+"F0.wireOp",EDGE,"E67"),sQuery(id+"F0.wireOp",EDGE,"E68"),sQuery(id+"F0.wireOp",EDGE,"E69"),sQuery(id+"F0.wireOp",EDGE,"E70"),sQuery(id+"F0.wireOp",EDGE,"E71"),sQuery(id+"F0.wireOp",EDGE,"E72"),sQuery(id+"F0.wireOp",EDGE,"E73"),sQuery(id+"F0.wireOp",EDGE,"E74"),sQuery(id+"F0.wireOp",EDGE,"E75"),sQuery(id+"F0.wireOp",EDGE,"E76"),sQuery(id+"F0.wireOp",EDGE,"E77"),sQuery(id+"F0.wireOp",EDGE,"E78"),sQuery(id+"F0.wireOp",EDGE,"E80"),sQuery(id+"F0.wireOp",EDGE,"E81"),sQuery(id+"F0.wireOp",EDGE,"E82"),sQuery(id+"F0.wireOp",EDGE,"E83"),sQuery(id+"F0.wireOp",EDGE,"E84"),sQuery(id+"F0.wireOp",EDGE,"E85"),sQuery(id+"F0.wireOp",EDGE,"E86"),sQuery(id+"F0.wireOp",EDGE,"E87"),sQuery(id+"F0.wireOp",EDGE,"E88"),sQuery(id+"F0.wireOp",EDGE,"E89"),sQuery(id+"F0.wireOp",EDGE,"E90"),sQuery(id+"F0.wireOp",EDGE,"E91"),sQuery(id+"F0.wireOp",EDGE,"E92"),sQuery(id+"F0.wireOp",EDGE,"E93"),sQuery(id+"F0.wireOp",EDGE,"E94"),sQuery(id+"F0.wireOp",EDGE,"E95"),sQuery(id+"F0.wireOp",EDGE,"E96"),sQuery(id+"F0.wireOp",EDGE,"E97"),sQuery(id+"F0.wireOp",EDGE,"E98"),sQuery(id+"F0.wireOp",EDGE,"E99"),sQuery(id+"F0.wireOp",EDGE,"E100"),sQuery(id+"F0.wireOp",EDGE,"E101"),sQuery(id+"F0.wireOp",EDGE,"E102"),sQuery(id+"F0.wireOp",EDGE,"E103"),sQuery(id+"F0.wireOp",EDGE,"E104"),sQuery(id+"F0.wireOp",EDGE,"E105"),sQuery(id+"F0.wireOp",EDGE,"E106"),sQuery(id+"F0.wireOp",EDGE,"E107"),sQuery(id+"F0.wireOp",EDGE,"E108"),sQuery(id+"F0.wireOp",EDGE,"E109"),sQuery(id+"F0.wireOp",EDGE,"E110"),sQuery(id+"F0.wireOp",EDGE,"E111"),sQuery(id+"F0.wireOp",EDGE,"E112"),sQuery(id+"F0.wireOp",EDGE,"E113"),sQuery(id+"F0.wireOp",EDGE,"E114"),sQuery(id+"F0.wireOp",EDGE,"E115"),sQuery(id+"F0.wireOp",EDGE,"E116"),sQuery(id+"F0.wireOp",EDGE,"E117"),sQuery(id+"F0.wireOp",EDGE,"E118"),sQuery(id+"F0.wireOp",EDGE,"E119"),sQuery(id+"F0.wireOp",EDGE,"E120"),sQuery(id+"F0.wireOp",EDGE,"E121"),sQuery(id+"F0.wireOp",EDGE,"E122"),sQuery(id+"F0.wireOp",EDGE,"E123"),sQuery(id+"F0.wireOp",EDGE,"E124"),sQuery(id+"F0.wireOp",EDGE,"E125"),sQuery(id+"F0.wireOp",EDGE,"E126"),sQuery(id+"F0.wireOp",EDGE,"E127"),sQuery(id+"F0.wireOp",EDGE,"E128"),sQuery(id+"F0.wireOp",EDGE,"E129"),sQuery(id+"F0.wireOp",EDGE,"E130"),sQuery(id+"F0.wireOp",EDGE,"E131"),sQuery(id+"F0.wireOp",EDGE,"E132"),sQuery(id+"F0.wireOp",EDGE,"E133"),sQuery(id+"F0.wireOp",EDGE,"E134"),sQuery(id+"F0.wireOp",EDGE,"E135"),sQuery(id+"F0.wireOp",EDGE,"E136"),sQuery(id+"F0.wireOp",EDGE,"E137"),sQuery(id+"F0.wireOp",EDGE,"E138"),sQuery(id+"F0.wireOp",EDGE,"E139"),sQuery(id+"F0.wireOp",EDGE,"E140"),sQuery(id+"F0.wireOp",EDGE,"E141"),sQuery(id+"F0.wireOp",EDGE,"E142"),sQuery(id+"F0.wireOp",EDGE,"E143"),sQuery(id+"F0.wireOp",EDGE,"E144"),sQuery(id+"F0.wireOp",EDGE,"E145"),sQuery(id+"F0.wireOp",EDGE,"E146"),sQuery(id+"F0.wireOp",EDGE,"E147"),sQuery(id+"F0.wireOp",EDGE,"E148"),sQuery(id+"F0.wireOp",EDGE,"E149"),sQuery(id+"F0.wireOp",EDGE,"E150"),sQuery(id+"F0.wireOp",EDGE,"E151"),sQuery(id+"F0.wireOp",EDGE,"E152"),sQuery(id+"F0.wireOp",EDGE,"E153"),sQuery(id+"F0.wireOp",EDGE,"E154"),sQuery(id+"F0.wireOp",EDGE,"E155"),sQuery(id+"F0.wireOp",EDGE,"E156"),sQuery(id+"F0.wireOp",EDGE,"E157"),sQuery(id+"F0.wireOp",EDGE,"E158"),sQuery(id+"F0.wireOp",EDGE,"E159"),sQuery(id+"F0.wireOp",EDGE,"E160"),sQuery(id+"F0.wireOp",EDGE,"E161"),sQuery(id+"F0.wireOp",EDGE,"E162"),sQuery(id+"F0.wireOp",EDGE,"E163"),sQuery(id+"F0.wireOp",EDGE,"E164"),sQuery(id+"F0.wireOp",EDGE,"E165"),sQuery(id+"F0.wireOp",EDGE,"E166"),sQuery(id+"F0.wireOp",EDGE,"E167"),sQuery(id+"F0.wireOp",EDGE,"E168"),sQuery(id+"F0.wireOp",EDGE,"E169"),sQuery(id+"F0.wireOp",EDGE,"E170"),sQuery(id+"F0.wireOp",EDGE,"E171"),sQuery(id+"F0.wireOp",EDGE,"E172"),sQuery(id+"F0.wireOp",EDGE,"E173"),sQuery(id+"F0.wireOp",EDGE,"E174"),sQuery(id+"F0.wireOp",EDGE,"E175"),sQuery(id+"F0.wireOp",EDGE,"E176"),sQuery(id+"F0.wireOp",EDGE,"E177"),sQuery(id+"F0.wireOp",EDGE,"E178"),sQuery(id+"F0.wireOp",EDGE,"E179"),sQuery(id+"F0.wireOp",EDGE,"E180"),sQuery(id+"F0.wireOp",EDGE,"E181"),sQuery(id+"F0.wireOp",EDGE,"E182"),sQuery(id+"F0.wireOp",EDGE,"E183"),sQuery(id+"F0.wireOp",EDGE,"E184"),sQuery(id+"F0.wireOp",EDGE,"E187"),sQuery(id+"F0.wireOp",EDGE,"E188")])],"isStart":false});
            var sketch = newSketch(context, id + "F4", { "sketchPlane" : qUnion([Q0])});
            skLineSegment(sketch, "E190.bottom", {"start": v(-90.49, -23.6) * mm, "end": v(90.49, -23.6) * mm});
            skLineSegment(sketch, "E190.top", {"start": v(-84.49, -61.6) * mm, "end": v(84.49, -61.6) * mm});
            skLineSegment(sketch, "E190.left", {"start": v(-90.49, -23.6) * mm, "end": v(-90.49, -55.6) * mm});
            skLineSegment(sketch, "E190.right", {"start": v(90.49, -23.6) * mm, "end": v(90.49, -55.6) * mm});
            skPoint(sketch, "E191.visualSharp", {"position": v(-90.49, -61.6) * mm});
            skArc(sketch, "E191.filletArc", {"start": v(-90.49, -55.6) * mm, "mid": v(-88.73, -59.84) * mm, "end": v(-84.49, -61.6) * mm});
            skPoint(sketch, "E192.visualSharp", {"position": v(90.49, -61.6) * mm});
            skArc(sketch, "E192.filletArc", {"start": v(84.49, -61.6) * mm, "mid": v(88.73, -59.84) * mm, "end": v(90.49, -55.6) * mm});
            skSolve(sketch);
        }
        {
            var Q0;
            Q0 = qSketchRegion(id + "F4", true);
            var Q1;
            Q1=makeQuery(id+"F1.opExtrude","CAP_FACE",FACE,{"disambiguationData":[OSD([sQuery(id+"F0.wireOp",EDGE,"E0"),sQuery(id+"F0.wireOp",EDGE,"E1"),sQuery(id+"F0.wireOp",EDGE,"E2"),sQuery(id+"F0.wireOp",EDGE,"E3"),sQuery(id+"F0.wireOp",EDGE,"E4"),sQuery(id+"F0.wireOp",EDGE,"E5"),sQuery(id+"F0.wireOp",EDGE,"E6"),sQuery(id+"F0.wireOp",EDGE,"E7"),sQuery(id+"F0.wireOp",EDGE,"E8"),sQuery(id+"F0.wireOp",EDGE,"E9"),sQuery(id+"F0.wireOp",EDGE,"E10"),sQuery(id+"F0.wireOp",EDGE,"E11"),sQuery(id+"F0.wireOp",EDGE,"E12"),sQuery(id+"F0.wireOp",EDGE,"E13"),sQuery(id+"F0.wireOp",EDGE,"E14"),sQuery(id+"F0.wireOp",EDGE,"E15"),sQuery(id+"F0.wireOp",EDGE,"E16"),sQuery(id+"F0.wireOp",EDGE,"E17"),sQuery(id+"F0.wireOp",EDGE,"E18"),sQuery(id+"F0.wireOp",EDGE,"E19"),sQuery(id+"F0.wireOp",EDGE,"E20"),sQuery(id+"F0.wireOp",EDGE,"E21"),sQuery(id+"F0.wireOp",EDGE,"E22"),sQuery(id+"F0.wireOp",EDGE,"E23"),sQuery(id+"F0.wireOp",EDGE,"E24"),sQuery(id+"F0.wireOp",EDGE,"E25"),sQuery(id+"F0.wireOp",EDGE,"E26"),sQuery(id+"F0.wireOp",EDGE,"E27"),sQuery(id+"F0.wireOp",EDGE,"E28"),sQuery(id+"F0.wireOp",EDGE,"E29"),sQuery(id+"F0.wireOp",EDGE,"E30"),sQuery(id+"F0.wireOp",EDGE,"E31"),sQuery(id+"F0.wireOp",EDGE,"E32"),sQuery(id+"F0.wireOp",EDGE,"E33"),sQuery(id+"F0.wireOp",EDGE,"E34"),sQuery(id+"F0.wireOp",EDGE,"E35"),sQuery(id+"F0.wireOp",EDGE,"E36"),sQuery(id+"F0.wireOp",EDGE,"E37"),sQuery(id+"F0.wireOp",EDGE,"E38"),sQuery(id+"F0.wireOp",EDGE,"E39"),sQuery(id+"F0.wireOp",EDGE,"E40"),sQuery(id+"F0.wireOp",EDGE,"E41"),sQuery(id+"F0.wireOp",EDGE,"E42"),sQuery(id+"F0.wireOp",EDGE,"E43"),sQuery(id+"F0.wireOp",EDGE,"E44"),sQuery(id+"F0.wireOp",EDGE,"E45"),sQuery(id+"F0.wireOp",EDGE,"E46"),sQuery(id+"F0.wireOp",EDGE,"E47"),sQuery(id+"F0.wireOp",EDGE,"E48"),sQuery(id+"F0.wireOp",EDGE,"E49"),sQuery(id+"F0.wireOp",EDGE,"E50"),sQuery(id+"F0.wireOp",EDGE,"E52"),sQuery(id+"F0.wireOp",EDGE,"E53"),sQuery(id+"F0.wireOp",EDGE,"E54"),sQuery(id+"F0.wireOp",EDGE,"E55"),sQuery(id+"F0.wireOp",EDGE,"E56"),sQuery(id+"F0.wireOp",EDGE,"E57"),sQuery(id+"F0.wireOp",EDGE,"E58"),sQuery(id+"F0.wireOp",EDGE,"E59"),sQuery(id+"F0.wireOp",EDGE,"E60"),sQuery(id+"F0.wireOp",EDGE,"E61"),sQuery(id+"F0.wireOp",EDGE,"E62"),sQuery(id+"F0.wireOp",EDGE,"E63"),sQuery(id+"F0.wireOp",EDGE,"E64"),sQuery(id+"F0.wireOp",EDGE,"E65"),sQuery(id+"F0.wireOp",EDGE,"E66"),sQuery(id+"F0.wireOp",EDGE,"E67"),sQuery(id+"F0.wireOp",EDGE,"E68"),sQuery(id+"F0.wireOp",EDGE,"E69"),sQuery(id+"F0.wireOp",EDGE,"E70"),sQuery(id+"F0.wireOp",EDGE,"E71"),sQuery(id+"F0.wireOp",EDGE,"E72"),sQuery(id+"F0.wireOp",EDGE,"E73"),sQuery(id+"F0.wireOp",EDGE,"E74"),sQuery(id+"F0.wireOp",EDGE,"E75"),sQuery(id+"F0.wireOp",EDGE,"E76"),sQuery(id+"F0.wireOp",EDGE,"E77"),sQuery(id+"F0.wireOp",EDGE,"E78"),sQuery(id+"F0.wireOp",EDGE,"E80"),sQuery(id+"F0.wireOp",EDGE,"E81"),sQuery(id+"F0.wireOp",EDGE,"E82"),sQuery(id+"F0.wireOp",EDGE,"E83"),sQuery(id+"F0.wireOp",EDGE,"E84"),sQuery(id+"F0.wireOp",EDGE,"E85"),sQuery(id+"F0.wireOp",EDGE,"E86"),sQuery(id+"F0.wireOp",EDGE,"E87"),sQuery(id+"F0.wireOp",EDGE,"E88"),sQuery(id+"F0.wireOp",EDGE,"E89"),sQuery(id+"F0.wireOp",EDGE,"E90"),sQuery(id+"F0.wireOp",EDGE,"E91"),sQuery(id+"F0.wireOp",EDGE,"E92"),sQuery(id+"F0.wireOp",EDGE,"E93"),sQuery(id+"F0.wireOp",EDGE,"E94"),sQuery(id+"F0.wireOp",EDGE,"E95"),sQuery(id+"F0.wireOp",EDGE,"E96"),sQuery(id+"F0.wireOp",EDGE,"E97"),sQuery(id+"F0.wireOp",EDGE,"E98"),sQuery(id+"F0.wireOp",EDGE,"E99"),sQuery(id+"F0.wireOp",EDGE,"E100"),sQuery(id+"F0.wireOp",EDGE,"E101"),sQuery(id+"F0.wireOp",EDGE,"E102"),sQuery(id+"F0.wireOp",EDGE,"E103"),sQuery(id+"F0.wireOp",EDGE,"E104"),sQuery(id+"F0.wireOp",EDGE,"E105"),sQuery(id+"F0.wireOp",EDGE,"E106"),sQuery(id+"F0.wireOp",EDGE,"E107"),sQuery(id+"F0.wireOp",EDGE,"E108"),sQuery(id+"F0.wireOp",EDGE,"E109"),sQuery(id+"F0.wireOp",EDGE,"E110"),sQuery(id+"F0.wireOp",EDGE,"E111"),sQuery(id+"F0.wireOp",EDGE,"E112"),sQuery(id+"F0.wireOp",EDGE,"E113"),sQuery(id+"F0.wireOp",EDGE,"E114"),sQuery(id+"F0.wireOp",EDGE,"E115"),sQuery(id+"F0.wireOp",EDGE,"E116"),sQuery(id+"F0.wireOp",EDGE,"E117"),sQuery(id+"F0.wireOp",EDGE,"E118"),sQuery(id+"F0.wireOp",EDGE,"E119"),sQuery(id+"F0.wireOp",EDGE,"E120"),sQuery(id+"F0.wireOp",EDGE,"E121"),sQuery(id+"F0.wireOp",EDGE,"E122"),sQuery(id+"F0.wireOp",EDGE,"E123"),sQuery(id+"F0.wireOp",EDGE,"E124"),sQuery(id+"F0.wireOp",EDGE,"E125"),sQuery(id+"F0.wireOp",EDGE,"E126"),sQuery(id+"F0.wireOp",EDGE,"E127"),sQuery(id+"F0.wireOp",EDGE,"E128"),sQuery(id+"F0.wireOp",EDGE,"E129"),sQuery(id+"F0.wireOp",EDGE,"E130"),sQuery(id+"F0.wireOp",EDGE,"E131"),sQuery(id+"F0.wireOp",EDGE,"E132"),sQuery(id+"F0.wireOp",EDGE,"E133"),sQuery(id+"F0.wireOp",EDGE,"E134"),sQuery(id+"F0.wireOp",EDGE,"E135"),sQuery(id+"F0.wireOp",EDGE,"E136"),sQuery(id+"F0.wireOp",EDGE,"E137"),sQuery(id+"F0.wireOp",EDGE,"E138"),sQuery(id+"F0.wireOp",EDGE,"E139"),sQuery(id+"F0.wireOp",EDGE,"E140"),sQuery(id+"F0.wireOp",EDGE,"E141"),sQuery(id+"F0.wireOp",EDGE,"E142"),sQuery(id+"F0.wireOp",EDGE,"E143"),sQuery(id+"F0.wireOp",EDGE,"E144"),sQuery(id+"F0.wireOp",EDGE,"E145"),sQuery(id+"F0.wireOp",EDGE,"E146"),sQuery(id+"F0.wireOp",EDGE,"E147"),sQuery(id+"F0.wireOp",EDGE,"E148"),sQuery(id+"F0.wireOp",EDGE,"E149"),sQuery(id+"F0.wireOp",EDGE,"E150"),sQuery(id+"F0.wireOp",EDGE,"E151"),sQuery(id+"F0.wireOp",EDGE,"E152"),sQuery(id+"F0.wireOp",EDGE,"E153"),sQuery(id+"F0.wireOp",EDGE,"E154"),sQuery(id+"F0.wireOp",EDGE,"E155"),sQuery(id+"F0.wireOp",EDGE,"E156"),sQuery(id+"F0.wireOp",EDGE,"E157"),sQuery(id+"F0.wireOp",EDGE,"E158"),sQuery(id+"F0.wireOp",EDGE,"E159"),sQuery(id+"F0.wireOp",EDGE,"E160"),sQuery(id+"F0.wireOp",EDGE,"E161"),sQuery(id+"F0.wireOp",EDGE,"E162"),sQuery(id+"F0.wireOp",EDGE,"E163"),sQuery(id+"F0.wireOp",EDGE,"E164"),sQuery(id+"F0.wireOp",EDGE,"E165"),sQuery(id+"F0.wireOp",EDGE,"E166"),sQuery(id+"F0.wireOp",EDGE,"E167"),sQuery(id+"F0.wireOp",EDGE,"E168"),sQuery(id+"F0.wireOp",EDGE,"E169"),sQuery(id+"F0.wireOp",EDGE,"E170"),sQuery(id+"F0.wireOp",EDGE,"E171"),sQuery(id+"F0.wireOp",EDGE,"E172"),sQuery(id+"F0.wireOp",EDGE,"E173"),sQuery(id+"F0.wireOp",EDGE,"E174"),sQuery(id+"F0.wireOp",EDGE,"E175"),sQuery(id+"F0.wireOp",EDGE,"E176"),sQuery(id+"F0.wireOp",EDGE,"E177"),sQuery(id+"F0.wireOp",EDGE,"E178"),sQuery(id+"F0.wireOp",EDGE,"E179"),sQuery(id+"F0.wireOp",EDGE,"E180"),sQuery(id+"F0.wireOp",EDGE,"E181"),sQuery(id+"F0.wireOp",EDGE,"E182"),sQuery(id+"F0.wireOp",EDGE,"E183"),sQuery(id+"F0.wireOp",EDGE,"E184"),sQuery(id+"F0.wireOp",EDGE,"E187"),sQuery(id+"F0.wireOp",EDGE,"E188")])],"isStart":true});
            extrude(context, id + "F5", {"entities" : qUnion([Q0]), "operationType" : NewBodyOperationType.ADD, "endBound" : BoundingType.UP_TO_SURFACE, "oppositeDirection" : true, "depth" : 25 * mm, "endBoundEntityFace" : qUnion([Q1]), "offsetDistance" : 25 * mm});
        }
        {
            var Q0;
            Q0=makeQuery(id+"F5.boolean.opBoolean","MERGE",FACE,{"derivedFrom":[makeQuery(id+"F1.opExtrude","CAP_FACE",FACE,{"disambiguationData":[OSD([sQuery(id+"F0.wireOp",EDGE,"E0"),sQuery(id+"F0.wireOp",EDGE,"E1"),sQuery(id+"F0.wireOp",EDGE,"E2"),sQuery(id+"F0.wireOp",EDGE,"E3"),sQuery(id+"F0.wireOp",EDGE,"E4"),sQuery(id+"F0.wireOp",EDGE,"E5"),sQuery(id+"F0.wireOp",EDGE,"E6"),sQuery(id+"F0.wireOp",EDGE,"E7"),sQuery(id+"F0.wireOp",EDGE,"E8"),sQuery(id+"F0.wireOp",EDGE,"E9"),sQuery(id+"F0.wireOp",EDGE,"E10"),sQuery(id+"F0.wireOp",EDGE,"E11"),sQuery(id+"F0.wireOp",EDGE,"E12"),sQuery(id+"F0.wireOp",EDGE,"E13"),sQuery(id+"F0.wireOp",EDGE,"E14"),sQuery(id+"F0.wireOp",EDGE,"E15"),sQuery(id+"F0.wireOp",EDGE,"E16"),sQuery(id+"F0.wireOp",EDGE,"E17"),sQuery(id+"F0.wireOp",EDGE,"E18"),sQuery(id+"F0.wireOp",EDGE,"E19"),sQuery(id+"F0.wireOp",EDGE,"E20"),sQuery(id+"F0.wireOp",EDGE,"E21"),sQuery(id+"F0.wireOp",EDGE,"E22"),sQuery(id+"F0.wireOp",EDGE,"E23"),sQuery(id+"F0.wireOp",EDGE,"E24"),sQuery(id+"F0.wireOp",EDGE,"E25"),sQuery(id+"F0.wireOp",EDGE,"E26"),sQuery(id+"F0.wireOp",EDGE,"E27"),sQuery(id+"F0.wireOp",EDGE,"E28"),sQuery(id+"F0.wireOp",EDGE,"E29"),sQuery(id+"F0.wireOp",EDGE,"E30"),sQuery(id+"F0.wireOp",EDGE,"E31"),sQuery(id+"F0.wireOp",EDGE,"E32"),sQuery(id+"F0.wireOp",EDGE,"E33"),sQuery(id+"F0.wireOp",EDGE,"E34"),sQuery(id+"F0.wireOp",EDGE,"E35"),sQuery(id+"F0.wireOp",EDGE,"E36"),sQuery(id+"F0.wireOp",EDGE,"E37"),sQuery(id+"F0.wireOp",EDGE,"E38"),sQuery(id+"F0.wireOp",EDGE,"E39"),sQuery(id+"F0.wireOp",EDGE,"E40"),sQuery(id+"F0.wireOp",EDGE,"E41"),sQuery(id+"F0.wireOp",EDGE,"E42"),sQuery(id+"F0.wireOp",EDGE,"E43"),sQuery(id+"F0.wireOp",EDGE,"E44"),sQuery(id+"F0.wireOp",EDGE,"E45"),sQuery(id+"F0.wireOp",EDGE,"E46"),sQuery(id+"F0.wireOp",EDGE,"E47"),sQuery(id+"F0.wireOp",EDGE,"E48"),sQuery(id+"F0.wireOp",EDGE,"E49"),sQuery(id+"F0.wireOp",EDGE,"E50"),sQuery(id+"F0.wireOp",EDGE,"E52"),sQuery(id+"F0.wireOp",EDGE,"E53"),sQuery(id+"F0.wireOp",EDGE,"E54"),sQuery(id+"F0.wireOp",EDGE,"E55"),sQuery(id+"F0.wireOp",EDGE,"E56"),sQuery(id+"F0.wireOp",EDGE,"E57"),sQuery(id+"F0.wireOp",EDGE,"E58"),sQuery(id+"F0.wireOp",EDGE,"E59"),sQuery(id+"F0.wireOp",EDGE,"E60"),sQuery(id+"F0.wireOp",EDGE,"E61"),sQuery(id+"F0.wireOp",EDGE,"E62"),sQuery(id+"F0.wireOp",EDGE,"E63"),sQuery(id+"F0.wireOp",EDGE,"E64"),sQuery(id+"F0.wireOp",EDGE,"E65"),sQuery(id+"F0.wireOp",EDGE,"E66"),sQuery(id+"F0.wireOp",EDGE,"E67"),sQuery(id+"F0.wireOp",EDGE,"E68"),sQuery(id+"F0.wireOp",EDGE,"E69"),sQuery(id+"F0.wireOp",EDGE,"E70"),sQuery(id+"F0.wireOp",EDGE,"E71"),sQuery(id+"F0.wireOp",EDGE,"E72"),sQuery(id+"F0.wireOp",EDGE,"E73"),sQuery(id+"F0.wireOp",EDGE,"E74"),sQuery(id+"F0.wireOp",EDGE,"E75"),sQuery(id+"F0.wireOp",EDGE,"E76"),sQuery(id+"F0.wireOp",EDGE,"E77"),sQuery(id+"F0.wireOp",EDGE,"E78"),sQuery(id+"F0.wireOp",EDGE,"E80"),sQuery(id+"F0.wireOp",EDGE,"E81"),sQuery(id+"F0.wireOp",EDGE,"E82"),sQuery(id+"F0.wireOp",EDGE,"E83"),sQuery(id+"F0.wireOp",EDGE,"E84"),sQuery(id+"F0.wireOp",EDGE,"E85"),sQuery(id+"F0.wireOp",EDGE,"E86"),sQuery(id+"F0.wireOp",EDGE,"E87"),sQuery(id+"F0.wireOp",EDGE,"E88"),sQuery(id+"F0.wireOp",EDGE,"E89"),sQuery(id+"F0.wireOp",EDGE,"E90"),sQuery(id+"F0.wireOp",EDGE,"E91"),sQuery(id+"F0.wireOp",EDGE,"E92"),sQuery(id+"F0.wireOp",EDGE,"E93"),sQuery(id+"F0.wireOp",EDGE,"E94"),sQuery(id+"F0.wireOp",EDGE,"E95"),sQuery(id+"F0.wireOp",EDGE,"E96"),sQuery(id+"F0.wireOp",EDGE,"E97"),sQuery(id+"F0.wireOp",EDGE,"E98"),sQuery(id+"F0.wireOp",EDGE,"E99"),sQuery(id+"F0.wireOp",EDGE,"E100"),sQuery(id+"F0.wireOp",EDGE,"E101"),sQuery(id+"F0.wireOp",EDGE,"E102"),sQuery(id+"F0.wireOp",EDGE,"E103"),sQuery(id+"F0.wireOp",EDGE,"E104"),sQuery(id+"F0.wireOp",EDGE,"E105"),sQuery(id+"F0.wireOp",EDGE,"E106"),sQuery(id+"F0.wireOp",EDGE,"E107"),sQuery(id+"F0.wireOp",EDGE,"E108"),sQuery(id+"F0.wireOp",EDGE,"E109"),sQuery(id+"F0.wireOp",EDGE,"E110"),sQuery(id+"F0.wireOp",EDGE,"E111"),sQuery(id+"F0.wireOp",EDGE,"E112"),sQuery(id+"F0.wireOp",EDGE,"E113"),sQuery(id+"F0.wireOp",EDGE,"E114"),sQuery(id+"F0.wireOp",EDGE,"E115"),sQuery(id+"F0.wireOp",EDGE,"E116"),sQuery(id+"F0.wireOp",EDGE,"E117"),sQuery(id+"F0.wireOp",EDGE,"E118"),sQuery(id+"F0.wireOp",EDGE,"E119"),sQuery(id+"F0.wireOp",EDGE,"E120"),sQuery(id+"F0.wireOp",EDGE,"E121"),sQuery(id+"F0.wireOp",EDGE,"E122"),sQuery(id+"F0.wireOp",EDGE,"E123"),sQuery(id+"F0.wireOp",EDGE,"E124"),sQuery(id+"F0.wireOp",EDGE,"E125"),sQuery(id+"F0.wireOp",EDGE,"E126"),sQuery(id+"F0.wireOp",EDGE,"E127"),sQuery(id+"F0.wireOp",EDGE,"E128"),sQuery(id+"F0.wireOp",EDGE,"E129"),sQuery(id+"F0.wireOp",EDGE,"E130"),sQuery(id+"F0.wireOp",EDGE,"E131"),sQuery(id+"F0.wireOp",EDGE,"E132"),sQuery(id+"F0.wireOp",EDGE,"E133"),sQuery(id+"F0.wireOp",EDGE,"E134"),sQuery(id+"F0.wireOp",EDGE,"E135"),sQuery(id+"F0.wireOp",EDGE,"E136"),sQuery(id+"F0.wireOp",EDGE,"E137"),sQuery(id+"F0.wireOp",EDGE,"E138"),sQuery(id+"F0.wireOp",EDGE,"E139"),sQuery(id+"F0.wireOp",EDGE,"E140"),sQuery(id+"F0.wireOp",EDGE,"E141"),sQuery(id+"F0.wireOp",EDGE,"E142"),sQuery(id+"F0.wireOp",EDGE,"E143"),sQuery(id+"F0.wireOp",EDGE,"E144"),sQuery(id+"F0.wireOp",EDGE,"E145"),sQuery(id+"F0.wireOp",EDGE,"E146"),sQuery(id+"F0.wireOp",EDGE,"E147"),sQuery(id+"F0.wireOp",EDGE,"E148"),sQuery(id+"F0.wireOp",EDGE,"E149"),sQuery(id+"F0.wireOp",EDGE,"E150"),sQuery(id+"F0.wireOp",EDGE,"E151"),sQuery(id+"F0.wireOp",EDGE,"E152"),sQuery(id+"F0.wireOp",EDGE,"E153"),sQuery(id+"F0.wireOp",EDGE,"E154"),sQuery(id+"F0.wireOp",EDGE,"E155"),sQuery(id+"F0.wireOp",EDGE,"E156"),sQuery(id+"F0.wireOp",EDGE,"E157"),sQuery(id+"F0.wireOp",EDGE,"E158"),sQuery(id+"F0.wireOp",EDGE,"E159"),sQuery(id+"F0.wireOp",EDGE,"E160"),sQuery(id+"F0.wireOp",EDGE,"E161"),sQuery(id+"F0.wireOp",EDGE,"E162"),sQuery(id+"F0.wireOp",EDGE,"E163"),sQuery(id+"F0.wireOp",EDGE,"E164"),sQuery(id+"F0.wireOp",EDGE,"E165"),sQuery(id+"F0.wireOp",EDGE,"E166"),sQuery(id+"F0.wireOp",EDGE,"E167"),sQuery(id+"F0.wireOp",EDGE,"E168"),sQuery(id+"F0.wireOp",EDGE,"E169"),sQuery(id+"F0.wireOp",EDGE,"E170"),sQuery(id+"F0.wireOp",EDGE,"E171"),sQuery(id+"F0.wireOp",EDGE,"E172"),sQuery(id+"F0.wireOp",EDGE,"E173"),sQuery(id+"F0.wireOp",EDGE,"E174"),sQuery(id+"F0.wireOp",EDGE,"E175"),sQuery(id+"F0.wireOp",EDGE,"E176"),sQuery(id+"F0.wireOp",EDGE,"E177"),sQuery(id+"F0.wireOp",EDGE,"E178"),sQuery(id+"F0.wireOp",EDGE,"E179"),sQuery(id+"F0.wireOp",EDGE,"E180"),sQuery(id+"F0.wireOp",EDGE,"E181"),sQuery(id+"F0.wireOp",EDGE,"E182"),sQuery(id+"F0.wireOp",EDGE,"E183"),sQuery(id+"F0.wireOp",EDGE,"E184"),sQuery(id+"F0.wireOp",EDGE,"E187"),sQuery(id+"F0.wireOp",EDGE,"E188")])],"isStart":false}),makeQuery(id+"F5.opExtrude","CAP_FACE",FACE,{"disambiguationData":[OSD([sQuery(id+"F4.wireOp",EDGE,"E190.bottom"),sQuery(id+"F4.wireOp",EDGE,"E190.top"),sQuery(id+"F4.wireOp",EDGE,"E190.left"),sQuery(id+"F4.wireOp",EDGE,"E190.right"),sQuery(id+"F4.wireOp",EDGE,"E191.filletArc"),sQuery(id+"F4.wireOp",EDGE,"E192.filletArc")])],"isStart":true})]});
            var sketch = newSketch(context, id + "F6", { "sketchPlane" : qUnion([Q0])});
            skText(sketch, "E193", { "text": "DL650", "fontName": "Tinos-Bold.ttf"});
            const initialGuessF6  = {"E193": [-0.00521, -0.0596, 1, 0, 0.015]};
            skSetInitialGuess(sketch, initialGuessF6);
            skSolve(sketch);
        }
        {
            var Q0;
            Q0 = qSketchRegion(id + "F6", true);
            extrude(context, id + "F7", {"entities" : qUnion([Q0]), "operationType" : NewBodyOperationType.ADD, "depth" : 1.4 * mm, "offsetDistance" : 25 * mm});
        }
        {
            var Q0;
            Q0=makeQuery(id+"F6.imprint","IMPRINT",FACE,{"disambiguationData":[TD([[makeQuery(id+"F6.imprint","IMPRINT",EDGE,{"derivedFrom":sQuery(id+"F6.wireOp",EDGE,"E193.sketch_text.stroke-8")}),1.0]])]});
            var sketch = newSketch(context, id + "F8", { "sketchPlane" : qUnion([Q0])});
            skLineSegment(sketch, "E194.bottom", {"start": v(-50.91, 72) * mm, "end": v(50.91, 72) * mm});
            skLineSegment(sketch, "E194.left", {"start": v(-56.91, 66) * mm, "end": v(-56.91, 59.95) * mm});
            skLineSegment(sketch, "E194.right", {"start": v(56.91, 66) * mm, "end": v(56.91, 59.95) * mm});
            skLineSegment(sketch, "E195", {"start": v(-87.31, 47.95) * mm, "end": v(-87.31, 31.3) * mm});
            skLineSegment(sketch, "E196", {"start": v(-62.91, 53.95) * mm, "end": v(-81.31, 53.95) * mm});
            skLineSegment(sketch, "E197", {"start": v(0, 0) * mm, "end": v(0, 26.7) * mm, "construction": true});
            skArc(sketch, "E198.0", {"start": v(-74.61, 44) * mm, "mid": v(-83.6, 40.29) * mm, "end": v(-87.31, 31.3) * mm});
            skLineSegment(sketch, "E199.0", {"start": v(-74.61, 44) * mm, "end": v(74.61, 44) * mm});
            skPoint(sketch, "E200.0", {"position": v(83.6, 40.29) * mm});
            skArc(sketch, "E201.0", {"start": v(87.31, 31.3) * mm, "mid": v(83.6, 40.29) * mm, "end": v(74.61, 44) * mm});
            skLineSegment(sketch, "E202.MirrorCS", {"start": v(87.31, 47.95) * mm, "end": v(87.31, 31.3) * mm});
            skLineSegment(sketch, "E203.MirrorCS", {"start": v(62.91, 53.95) * mm, "end": v(81.31, 53.95) * mm});
            skPoint(sketch, "E204.visualSharp", {"position": v(-56.91, 53.95) * mm});
            skArc(sketch, "E204.filletArc", {"start": v(-62.91, 53.95) * mm, "mid": v(-58.67, 55.71) * mm, "end": v(-56.91, 59.95) * mm});
            skPoint(sketch, "E205.visualSharp", {"position": v(-87.31, 53.95) * mm});
            skArc(sketch, "E205.filletArc", {"start": v(-81.31, 53.95) * mm, "mid": v(-85.56, 52.2) * mm, "end": v(-87.31, 47.95) * mm});
            skPoint(sketch, "E206.visualSharp", {"position": v(56.91, 53.95) * mm});
            skArc(sketch, "E206.filletArc", {"start": v(56.91, 59.95) * mm, "mid": v(58.67, 55.71) * mm, "end": v(62.91, 53.95) * mm});
            skPoint(sketch, "E207.visualSharp", {"position": v(87.31, 53.95) * mm});
            skArc(sketch, "E207.filletArc", {"start": v(87.31, 47.95) * mm, "mid": v(85.56, 52.2) * mm, "end": v(81.31, 53.95) * mm});
            skPoint(sketch, "E208.visualSharp", {"position": v(-56.91, 72) * mm});
            skArc(sketch, "E208.filletArc", {"start": v(-50.91, 72) * mm, "mid": v(-55.16, 70.25) * mm, "end": v(-56.91, 66) * mm});
            skPoint(sketch, "E209.visualSharp", {"position": v(56.91, 72) * mm});
            skArc(sketch, "E209.filletArc", {"start": v(56.91, 66) * mm, "mid": v(55.16, 70.25) * mm, "end": v(50.91, 72) * mm});
            skSolve(sketch);
        }
        {
            var Q0;
            Q0 = qSketchRegion(id + "F8", true);
            extrude(context, id + "F9", {"entities" : qUnion([Q0]), "operationType" : NewBodyOperationType.REMOVE, "oppositeDirection" : true, "depth" : 25 * mm, "offsetDistance" : 25 * mm});
        }
    });
